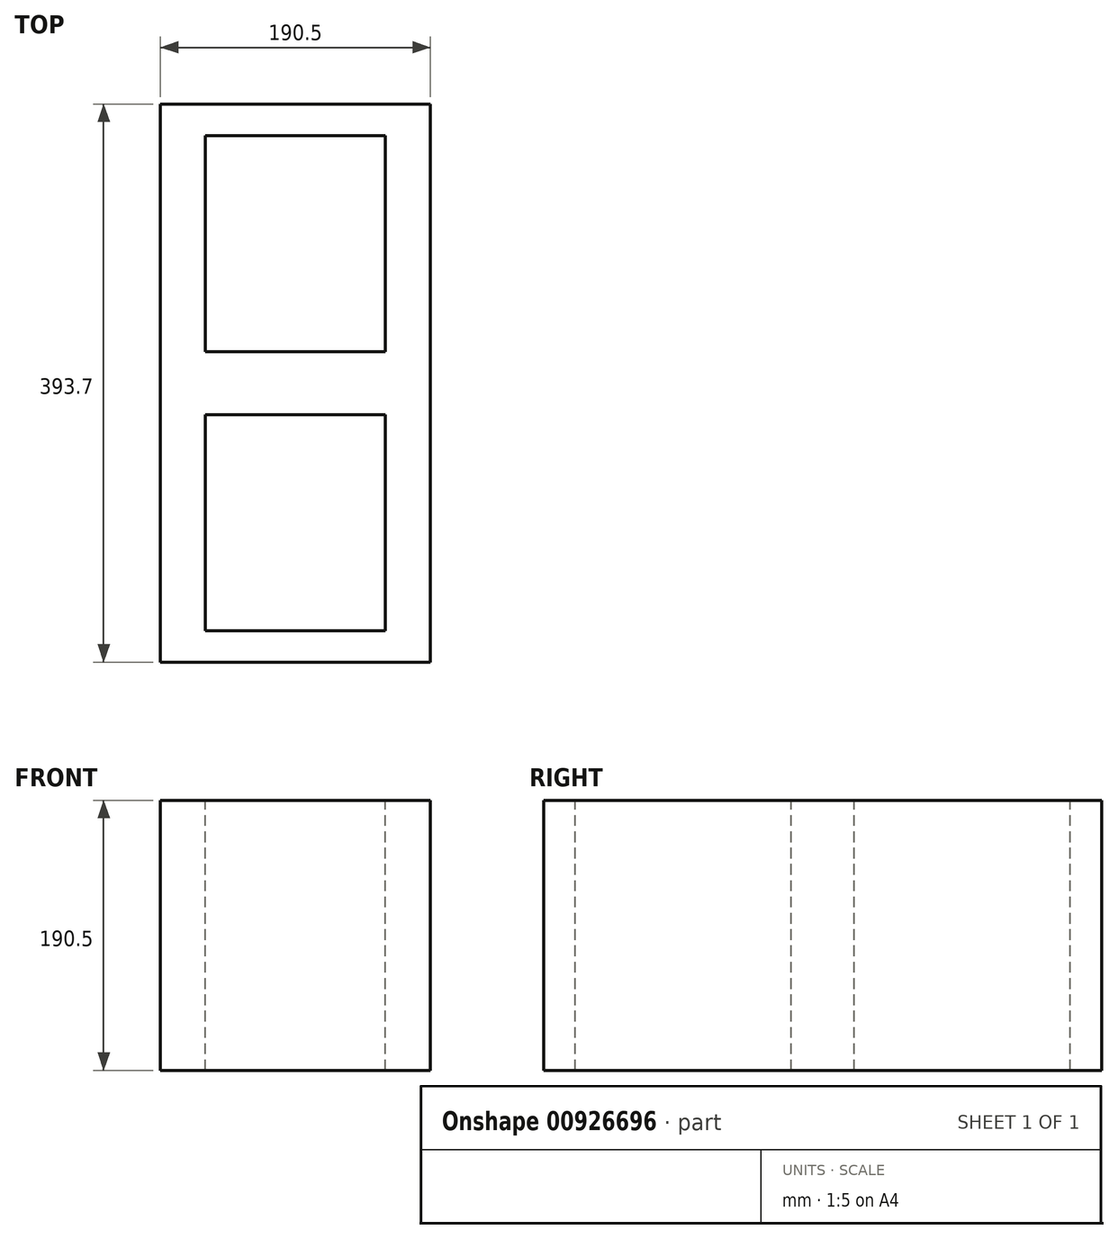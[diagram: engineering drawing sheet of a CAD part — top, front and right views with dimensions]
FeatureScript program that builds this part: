
annotation { "Feature Type Name" : "Feature", "Feature Type Description" : "" }
export const myFeature = defineFeature(function(context is Context, id is Id, definition is map)
    precondition{}
    {
        {
            var Q0;
            Q0=qCreatedBy(makeId("Top.planeOp"),FACE);
            var sketch = newSketch(context, id + "F0", { "sketchPlane" : qUnion([Q0])});
            skLineSegment(sketch, "E0.bottom", {"start": v(0, 0) * mm, "end": v(190.5, 0) * mm});
            skLineSegment(sketch, "E0.top", {"start": v(0, 393.7) * mm, "end": v(190.5, 393.7) * mm});
            skLineSegment(sketch, "E0.left", {"start": v(0, 0) * mm, "end": v(0, 393.7) * mm});
            skLineSegment(sketch, "E0.right", {"start": v(190.5, 0) * mm, "end": v(190.5, 393.7) * mm});
            skSolve(sketch);
        }
        {
            var Q0;
            Q0 = qSketchRegion(id + "F0", true);
            extrude(context, id + "F1", {"entities" : qUnion([Q0]), "depth" : 190.5 * mm, "offsetDistance" : 25.4 * mm});
        }
        {
            var Q0;
            Q0=makeQuery(id+"F1.opExtrude","CAP_FACE",FACE,{"disambiguationData":[OSD([sQuery(id+"F0.wireOp",EDGE,"E0.bottom"),sQuery(id+"F0.wireOp",EDGE,"E0.top"),sQuery(id+"F0.wireOp",EDGE,"E0.left"),sQuery(id+"F0.wireOp",EDGE,"E0.right")])],"isStart":false});
            var sketch = newSketch(context, id + "F2", { "sketchPlane" : qUnion([Q0])});
            skLineSegment(sketch, "E1", {"start": v(0, 196.85) * mm, "end": v(190.5, 196.85) * mm, "construction": true});
            skLineSegment(sketch, "E2", {"start": v(95.25, 393.7) * mm, "end": v(95.25, 0) * mm, "construction": true});
            skLineSegment(sketch, "E3", {"start": v(0, 295.28) * mm, "end": v(190.5, 295.28) * mm, "construction": true});
            skLineSegment(sketch, "E4.bottom", {"start": v(31.75, 371.48) * mm, "end": v(158.75, 371.48) * mm});
            skLineSegment(sketch, "E4.top", {"start": v(31.75, 219.08) * mm, "end": v(158.75, 219.08) * mm});
            skLineSegment(sketch, "E4.left", {"start": v(31.75, 371.48) * mm, "end": v(31.75, 219.08) * mm});
            skLineSegment(sketch, "E4.right", {"start": v(158.75, 371.48) * mm, "end": v(158.75, 219.08) * mm});
            skPoint(sketch, "E4.middle", {"position": v(95.25, 295.28) * mm});
            skLineSegment(sketch, "E5.MirrorCS", {"start": v(31.75, 22.23) * mm, "end": v(31.75, 174.62) * mm});
            skLineSegment(sketch, "E6.MirrorCS", {"start": v(31.75, 174.62) * mm, "end": v(158.75, 174.63) * mm});
            skLineSegment(sketch, "E7.MirrorCS", {"start": v(158.75, 22.23) * mm, "end": v(158.75, 174.62) * mm});
            skLineSegment(sketch, "E8.MirrorCS", {"start": v(31.75, 22.23) * mm, "end": v(158.75, 22.23) * mm});
            skSolve(sketch);
        }
        {
            var Q0;
            Q0=makeQuery(id+"F2.imprint","IMPRINT",FACE,{"disambiguationData":[TD([[makeQuery(id+"F2.imprint","IMPRINT",EDGE,{"derivedFrom":sQuery(id+"F2.wireOp",EDGE,"E5.MirrorCS")}),-1.0]])]});
            var Q1;
            Q1=makeQuery(id+"F2.imprint","IMPRINT",FACE,{"disambiguationData":[TD([[makeQuery(id+"F2.imprint","IMPRINT",EDGE,{"derivedFrom":sQuery(id+"F2.wireOp",EDGE,"E4.bottom")}),-1.0]])]});
            extrude(context, id + "F3", {"entities" : qUnion([Q0, Q1]), "operationType" : NewBodyOperationType.REMOVE, "endBound" : BoundingType.THROUGH_ALL, "oppositeDirection" : true, "depth" : 25.4 * mm, "offsetDistance" : 25.4 * mm});
        }
    });
